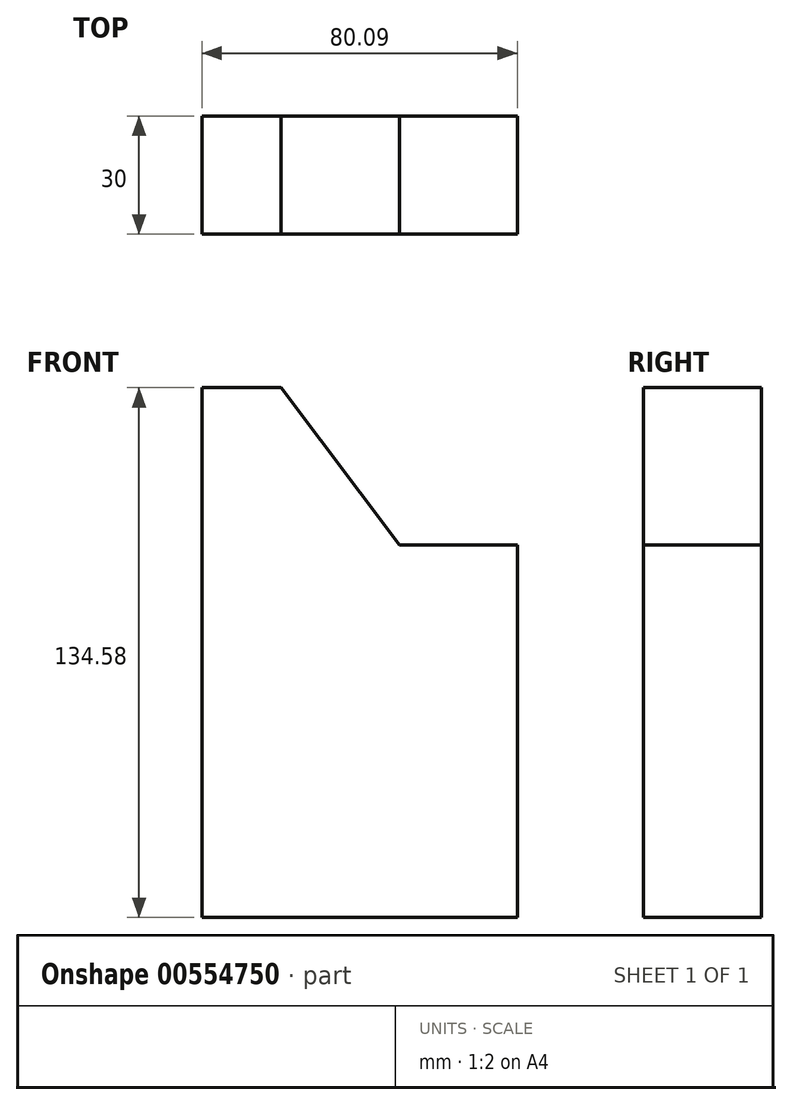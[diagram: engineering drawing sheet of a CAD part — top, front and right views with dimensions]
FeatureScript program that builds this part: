
annotation { "Feature Type Name" : "Feature", "Feature Type Description" : "" }
export const myFeature = defineFeature(function(context is Context, id is Id, definition is map)
    precondition{}
    {
        {
            var Q0;
            Q0=qCreatedBy(makeId("Front.planeOp"),FACE);
            var sketch = newSketch(context, id + "F0", { "sketchPlane" : qUnion([Q0])});
            skLineSegment(sketch, "E0", {"start": v(-68.99, -62.11) * mm, "end": v(11.1, -62.11) * mm});
            skLineSegment(sketch, "E1", {"start": v(11.1, -62.11) * mm, "end": v(11.1, 32.54) * mm});
            skLineSegment(sketch, "E2", {"start": v(11.1, 32.54) * mm, "end": v(-18.9, 32.54) * mm});
            skLineSegment(sketch, "E3", {"start": v(-18.9, 32.54) * mm, "end": v(-48.99, 72.47) * mm});
            skLineSegment(sketch, "E4", {"start": v(-48.99, 72.47) * mm, "end": v(-68.99, 72.47) * mm});
            skLineSegment(sketch, "E5", {"start": v(-68.99, 72.47) * mm, "end": v(-68.99, -62.11) * mm});
            skLineSegment(sketch, "E6", {"start": v(-48.99, 72.47) * mm, "end": v(-48.99, 43.3) * mm});
            skLineSegment(sketch, "E7", {"start": v(-18.9, 32.54) * mm, "end": v(-27.55, 32.54) * mm});
            skSolve(sketch);
        }
        {
            var Q0;
            Q0 = qSketchRegion(id + "F0", true);
            extrude(context, id + "F1", {"entities" : qUnion([Q0]), "depth" : 30 * mm, "offsetDistance" : 25 * mm});
        }
    });
